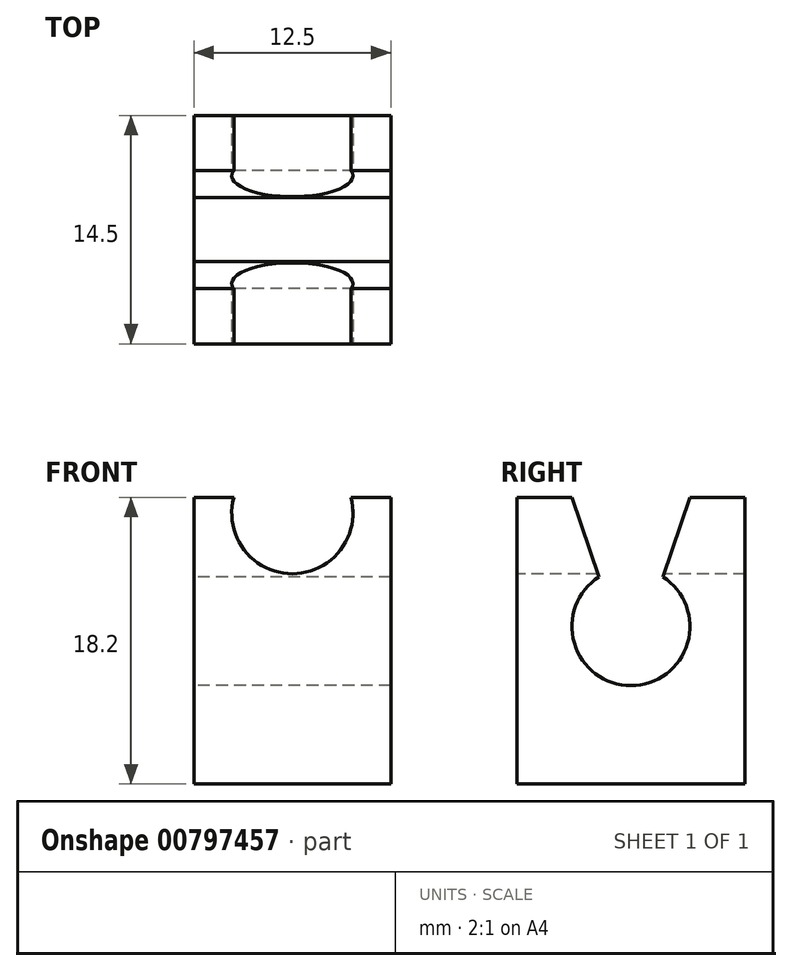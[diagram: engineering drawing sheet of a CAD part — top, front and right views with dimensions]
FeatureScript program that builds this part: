
annotation { "Feature Type Name" : "Feature", "Feature Type Description" : "" }
export const myFeature = defineFeature(function(context is Context, id is Id, definition is map)
    precondition{}
    {
        {
            var Q0;
            Q0=qCreatedBy(makeId("Top.planeOp"),FACE);
            var sketch = newSketch(context, id + "F0", { "sketchPlane" : qUnion([Q0])});
            skLineSegment(sketch, "E0.bottom", {"start": v(0, 0) * mm, "end": v(12.5, 0) * mm});
            skLineSegment(sketch, "E0.top", {"start": v(0, 14.5) * mm, "end": v(12.5, 14.5) * mm});
            skLineSegment(sketch, "E0.left", {"start": v(0, 0) * mm, "end": v(0, 14.5) * mm});
            skLineSegment(sketch, "E0.right", {"start": v(12.5, 0) * mm, "end": v(12.5, 14.5) * mm});
            skSolve(sketch);
        }
        {
            var Q0;
            Q0 = qSketchRegion(id + "F0", true);
            extrude(context, id + "F1", {"entities" : qUnion([Q0]), "depth" : 18.2 * mm, "offsetDistance" : 25 * mm});
        }
        {
            var Q0;
            Q0=makeQuery(id+"F1.opExtrude","SWEPT_FACE",FACE,{"disambiguationData":[OSD([sQuery(id+"F0.wireOp",EDGE,"E0.bottom")])]});
            var sketch = newSketch(context, id + "F2", { "sketchPlane" : qUnion([Q0])});
            skCircle(sketch, "E1", {"center": v(6.25, 17.2) * mm, "radius": 3.85 * mm});
            skPoint(sketch, "E1.centerSnap0", {"position": v(6.25, 18.2) * mm});
            skSolve(sketch);
        }
        {
            var Q0;
            Q0 = qSketchRegion(id + "F2", true);
            extrude(context, id + "F3", {"entities" : qUnion([Q0]), "operationType" : NewBodyOperationType.REMOVE, "oppositeDirection" : true, "depth" : 25 * mm, "offsetDistance" : 25 * mm});
        }
        {
            var Q0;
            Q0=makeQuery(id+"F1.opExtrude","SWEPT_FACE",FACE,{"disambiguationData":[OSD([sQuery(id+"F0.wireOp",EDGE,"E0.left")])]});
            var sketch = newSketch(context, id + "F4", { "sketchPlane" : qUnion([Q0])});
            skArc(sketch, "E2", {"start": v(-9.28, 13.15) * mm, "mid": v(-7.25, 6.25) * mm, "end": v(-5.22, 13.15) * mm});
            skPoint(sketch, "E2.centerSnap0", {"position": v(-7.25, 18.2) * mm});
            skLineSegment(sketch, "E3", {"start": v(-9.28, 13.15) * mm, "end": v(-11, 18.2) * mm});
            skLineSegment(sketch, "E4", {"start": v(-5.22, 13.15) * mm, "end": v(-3.5, 18.2) * mm});
            skLineSegment(sketch, "E5", {"start": v(-3.5, 18.2) * mm, "end": v(-11, 18.2) * mm});
            skSolve(sketch);
        }
        {
            var Q0;
            Q0 = qSketchRegion(id + "F4", true);
            extrude(context, id + "F5", {"entities" : qUnion([Q0]), "operationType" : NewBodyOperationType.REMOVE, "oppositeDirection" : true, "depth" : 25 * mm, "offsetDistance" : 25 * mm});
        }
    });
